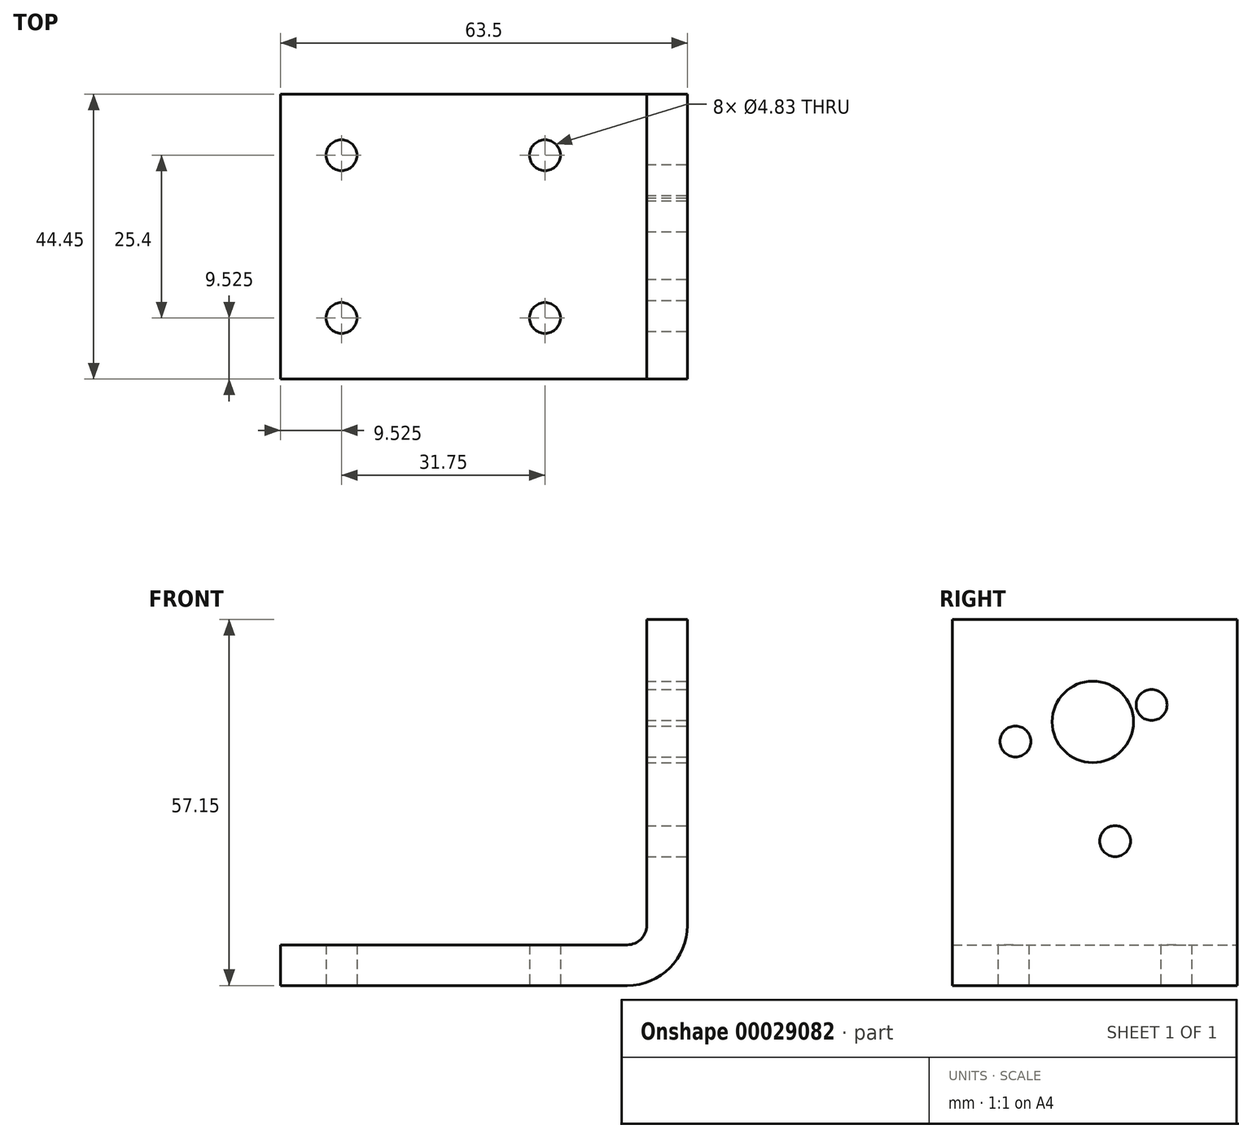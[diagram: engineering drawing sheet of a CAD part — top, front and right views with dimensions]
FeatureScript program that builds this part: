
annotation { "Feature Type Name" : "Feature", "Feature Type Description" : "" }
export const myFeature = defineFeature(function(context is Context, id is Id, definition is map)
    precondition{}
    {
        {
            var Q0;
            Q0=qCreatedBy(makeId("Front.planeOp"),FACE);
            var sketch = newSketch(context, id + "F0", { "sketchPlane" : qUnion([Q0])});
            skLineSegment(sketch, "E0", {"start": v(-63.5, 0) * mm, "end": v(0, 0) * mm});
            skLineSegment(sketch, "E1", {"start": v(0, 0) * mm, "end": v(0, 57.15) * mm});
            skLineSegment(sketch, "E2", {"start": v(-63.5, 0) * mm, "end": v(-63.5, 6.35) * mm});
            skLineSegment(sketch, "E3", {"start": v(-63.5, 6.35) * mm, "end": v(-6.35, 6.35) * mm});
            skLineSegment(sketch, "E4", {"start": v(0, 57.15) * mm, "end": v(-6.35, 57.15) * mm});
            skLineSegment(sketch, "E5", {"start": v(-6.35, 57.15) * mm, "end": v(-6.35, 6.35) * mm});
            skSolve(sketch);
        }
        {
            var Q0;
            Q0=makeQuery(id+"F0.imprint","IMPRINT",FACE,{"disambiguationData":[TD([[makeQuery(id+"F0.imprint","IMPRINT",EDGE,{"derivedFrom":sQuery(id+"F0.wireOp",EDGE,"E0")}),1.0]])]});
            extrude(context, id + "F1", {"entities" : qUnion([Q0]), "depth" : 44.45 * mm});
        }
        {
            var Q0;
            Q0=makeQuery(id+"F1.opExtrude","SWEPT_EDGE",EDGE,{"disambiguationData":[OSD([sQuery(id+"F0.wireOp",EDGE,"E0"),sQuery(id+"F0.wireOp",EDGE,"E1")])]});
            fillet(context, id + "F2", {"entities" : qUnion([Q0]), "radius" : 9.4 * mm, "tangentPropagation" : true, "allowEdgeOverflow" : false});
        }
        {
            var Q0;
            Q0=makeQuery(id+"F1.opExtrude","SWEPT_EDGE",EDGE,{"disambiguationData":[OSD([sQuery(id+"F0.wireOp",EDGE,"E3"),sQuery(id+"F0.wireOp",EDGE,"E5")])]});
            fillet(context, id + "F3", {"entities" : qUnion([Q0]), "radius" : 3.05 * mm, "tangentPropagation" : true, "allowEdgeOverflow" : false});
        }
        {
            var Q0;
            Q0=qCreatedBy(makeId("Right.planeOp"),FACE);
            var sketch = newSketch(context, id + "F4", { "sketchPlane" : qUnion([Q0])});
            skCircle(sketch, "E6", {"center": v(-13.37, 43.78) * mm, "radius": 2.41 * mm});
            skLineSegment(sketch, "E7", {"start": v(-22.35, 34.8) * mm, "end": v(-22.35, -6.3) * mm, "construction": true});
            skLineSegment(sketch, "E8", {"start": v(-22.35, 34.8) * mm, "end": v(-18.68, 21.1) * mm, "construction": true});
            skLineSegment(sketch, "E9", {"start": v(-22.35, 34.8) * mm, "end": v(-37.3, 38.8) * mm, "construction": true});
            skLineSegment(sketch, "E10", {"start": v(-22.35, 34.8) * mm, "end": v(-52.84, 34.8) * mm, "construction": true});
            skLineSegment(sketch, "E11", {"start": v(-22.35, 34.8) * mm, "end": v(5.4, 34.8) * mm, "construction": true});
            skCircle(sketch, "E12", {"center": v(-34.62, 38.09) * mm, "radius": 2.41 * mm});
            skCircle(sketch, "E13", {"center": v(-19.06, 22.53) * mm, "radius": 2.41 * mm});
            skCircle(sketch, "E14", {"center": v(-22.54, 41.15) * mm, "radius": 6.35 * mm});
            skSolve(sketch);
        }
        {
            var Q0;
            Q0=makeQuery(id+"F4.imprint","IMPRINT",FACE,{"disambiguationData":[TD([[makeQuery(id+"F4.imprint","IMPRINT",EDGE,{"derivedFrom":sQuery(id+"F4.wireOp",EDGE,"E14")}),1.0]])]});
            var Q1;
            Q1=makeQuery(id+"F4.imprint","IMPRINT",FACE,{"disambiguationData":[TD([[makeQuery(id+"F4.imprint","IMPRINT",EDGE,{"derivedFrom":sQuery(id+"F4.wireOp",EDGE,"E6")}),1.0]])]});
            var Q2;
            Q2=makeQuery(id+"F4.imprint","IMPRINT",FACE,{"disambiguationData":[TD([[makeQuery(id+"F4.imprint","IMPRINT",EDGE,{"derivedFrom":sQuery(id+"F4.wireOp",EDGE,"E13")}),1.0]])]});
            var Q3;
            Q3=makeQuery(id+"F4.imprint","IMPRINT",FACE,{"disambiguationData":[TD([[makeQuery(id+"F4.imprint","IMPRINT",EDGE,{"derivedFrom":sQuery(id+"F4.wireOp",EDGE,"E12")}),1.0]])]});
            extrude(context, id + "F5", {"entities" : qUnion([Q0, Q1, Q2, Q3]), "operationType" : NewBodyOperationType.REMOVE, "oppositeDirection" : true, "depth" : 25.4 * mm});
        }
        {
            var Q0;
            Q0=makeQuery(id+"F1.opExtrude","SWEPT_FACE",FACE,{"disambiguationData":[OSD([sQuery(id+"F0.wireOp",EDGE,"E0")])]});
            var sketch = newSketch(context, id + "F6", { "sketchPlane" : qUnion([Q0])});
            skCircle(sketch, "E15", {"center": v(-22.23, 9.53) * mm, "radius": 2.41 * mm});
            skCircle(sketch, "E16", {"center": v(-22.23, 34.93) * mm, "radius": 2.41 * mm});
            skCircle(sketch, "E17", {"center": v(-53.98, 9.53) * mm, "radius": 2.41 * mm});
            skCircle(sketch, "E18", {"center": v(-53.98, 34.93) * mm, "radius": 2.41 * mm});
            skSolve(sketch);
        }
        {
            var Q0;
            Q0=makeQuery(id+"F6.imprint","IMPRINT",FACE,{"disambiguationData":[TD([[makeQuery(id+"F6.imprint","IMPRINT",EDGE,{"derivedFrom":sQuery(id+"F6.wireOp",EDGE,"E18")}),1.0]])]});
            var Q1;
            Q1=makeQuery(id+"F6.imprint","IMPRINT",FACE,{"disambiguationData":[TD([[makeQuery(id+"F6.imprint","IMPRINT",EDGE,{"derivedFrom":sQuery(id+"F6.wireOp",EDGE,"E17")}),1.0]])]});
            var Q2;
            Q2=makeQuery(id+"F6.imprint","IMPRINT",FACE,{"disambiguationData":[TD([[makeQuery(id+"F6.imprint","IMPRINT",EDGE,{"derivedFrom":sQuery(id+"F6.wireOp",EDGE,"E15")}),1.0]])]});
            var Q3;
            Q3=makeQuery(id+"F6.imprint","IMPRINT",FACE,{"disambiguationData":[TD([[makeQuery(id+"F6.imprint","IMPRINT",EDGE,{"derivedFrom":sQuery(id+"F6.wireOp",EDGE,"E16")}),1.0]])]});
            extrude(context, id + "F7", {"entities" : qUnion([Q0, Q1, Q2, Q3]), "operationType" : NewBodyOperationType.REMOVE, "endBound" : BoundingType.THROUGH_ALL, "oppositeDirection" : true, "depth" : 25.4 * mm});
        }
    });
